# Revit family: 26-35-0095-DN40-300
name_source: partatom
category: Pipe Accessories
units: mm (PartAtom-declared; Revit-internal decimal feet)

## family parameters
Always vertical = No
Cut with Voids When Loaded = No
OmniClass Number = 23.60.00.00
OmniClass Title = General Purpose: Services
Part Type = Valve - Breaks Into
Round Connector Dimension = Use Diameter
Shared = Yes
Work Plane-Based = No

## types (10) — shared parameters
Body_Wallthickness = 15 mm  [stored 0.0492126 ft]
DN040_PN10/16 = 26-040-35-0147099
DN050_PN10/16 = 26-050-35-0147099
DN065_PN10/16 = 26-065-35-0147099
DN080_PN10/16 = 26-080-35-0147099
DN100_PN10/16 = 26-100-35-0147099
DN125_PN10/16 = 26-125-35-0147099
DN150_PN10/16 = 26-150-35-0147099
DN200_PN10 = 26-200-35-0047099
DN200_PN16 = 26-200-35-0147099
DN250_PN10 = 26-250-35-007
DN250_PN16 = 26-250-35-017
DN300_PN10 = 26-300-35-007
DN300_PN16 = 26-300-35-017
Ftc = 4 mm  [stored 0.0131234 ft]
Name_Height_reference = 10 mm  [stored 0.0328084 ft]
Rib_Height_Reference_3 = 100 mm
Rib_Thickness = 18 mm  [stored 0.0590551 ft]
Search_table = 26-35-0095-DN40-300
Tf = 26 mm
URL product pages = https://www.avkvalves.com
zero-valued in all types: Bottom_Reference

## per-type parameters (varying)
- DN 050: At=60.5 mm; Body_Height=110 mm; Body_depth=121 mm; Body_width=74 mm; Bonnet_Flange_Depth=130 mm; Bonnet_Flange_Width=90 mm; Bonnet_Flange_cut=7.5 mm  [stored 0.0246063 ft]; Bonnet_Flange_thickness=15 mm  [stored 0.0492126 ft]; Bonnet_Height=41.25 mm; Bonnet_Reference_height=100 mm; Bonnet_Thickness=75.48 mm; Bt=75.48 mm; Bt_2=68 mm; CL=56 mm; CL _Thickness=12 mm  [stored 0.0393701 ft]; CL_2=26 mm; CL_Thickness 2=20 mm  [stored 0.0656168 ft]; Cut_Reference=300 mm; DN 050=Yes; DN 065=No; DN 080=No; DN 100=No; DN 125=No; DN 150=No; DN 200=No; DN 250=No; DN 300=No; Description_=AVK_GATE_VALVE,FLANGED; F=7 mm  [stored 0.0229659 ft]; F1=8 mm  [stored 0.0262467 ft]; F2=30 mm; Fillet_Thickness=6 mm  [stored 0.019685 ft]; Flange_OR=82.5 mm; Flange_Thickness=19 mm  [stored 0.062336 ft]; Flange_Thickness_cut=28.75 mm; Ftc_reference_height=82.5 mm; Gearbox_Flange_Dia=12 mm  [stored 0.0393701 ft]; Gearbox_Flangethickness=12 mm  [stored 0.0393701 ft]; H=208 mm; H3=294 mm; Horizontal_Flange_width=172 mm; ID (Radius)=25 mm  [stored 0.082021 ft]; L=150 mm; L_Dia=50 mm; Name_Reference=90 mm; Name_Width=37 mm; Nominal Diameter (DN)=50 mm; R1tv=825 mm; R2f=15 mm  [stored 0.0492126 ft]; RF_Dia=50 mm; Rf=286.67 mm; Rib_Height_Reference_1=120 mm; Rib_Height_Reference_2=110 mm; Rib_Height_Reference_4=60 mm; Rib_Width_1=37 mm; Rib_Width_2=37 mm; Rib_Width_3=37 mm; Rib_depth_1=37 mm; Rib_depth_2=37 mm; Rib_depth_3=37 mm; Rt=275 mm
- DN 065: At=54.5 mm; Body_Height=140 mm; Body_depth=109 mm; Body_width=74 mm; Bonnet_Flange_Depth=135 mm; Bonnet_Flange_Width=85 mm; Bonnet_Flange_cut=7.5 mm  [stored 0.0246063 ft]; Bonnet_Flange_thickness=15 mm  [stored 0.0492126 ft]; Bonnet_Height=46.25 mm; Bonnet_Reference_height=130 mm; Bonnet_Thickness=75.48 mm; Bt=75.48 mm; Bt_2=68 mm; CL=59.83 mm; CL _Thickness=11.17 mm; CL_2=29.83 mm; CL_Thickness 2=18.33 mm; Cut_Reference=340 mm; DN 050=No; DN 065=Yes; DN 080=Yes; DN 100=Yes; DN 125=Yes; DN 150=Yes; DN 200=Yes; DN 250=Yes; DN 300=Yes; Description_=AVK_GATE-VALVE,FLANGED; F=8.5 mm; F1=10 mm  [stored 0.0328084 ft]; F2=34 mm; Fillet_Thickness=6 mm  [stored 0.019685 ft]; Flange_OR=92.5 mm; Flange_Thickness=19 mm  [stored 0.062336 ft]; Flange_Thickness_cut=30 mm; Ftc_reference_height=92.5 mm; Gearbox_Flange_Dia=11.17 mm; Gearbox_Flangethickness=11.17 mm; H=245 mm; H3=338 mm; Horizontal_Flange_width=186 mm; ID (Radius)=32.5 mm; L=170 mm; L_Dia=65 mm; Name_Reference=100 mm; Name_Width=37 mm; Nominal Diameter (DN)=65 mm; R1tv=925 mm; R2f=15 mm  [stored 0.0492126 ft]; RF_Dia=59 mm; Rf=310 mm; Rib_Height_Reference_1=120 mm; Rib_Height_Reference_2=110 mm; Rib_Height_Reference_4=75 mm; Rib_Width_1=37 mm; Rib_Width_2=37 mm; Rib_Width_3=37 mm; Rib_depth_1=37 mm; Rib_depth_2=37 mm; Rib_depth_3=37 mm; Rt=308.33 mm
- DN 080: At=72.5 mm; Body_Height=155 mm; Body_depth=145 mm; Body_width=79 mm; Bonnet_Flange_Depth=150 mm; Bonnet_Flange_Width=100 mm; Bonnet_Flange_cut=7.5 mm  [stored 0.0246063 ft]; Bonnet_Flange_thickness=15 mm  [stored 0.0492126 ft]; Bonnet_Height=50 mm; Bonnet_Reference_height=145 mm; Bonnet_Thickness=80.58 mm; Bt=80.58 mm; Bt_2=73 mm; CL=79.33 mm; CL _Thickness=13.67 mm; CL_2=49.33 mm; CL_Thickness 2=23.33 mm; Cut_Reference=360 mm; DN 050=Yes; DN 065=Yes; DN 080=Yes; DN 100=Yes; DN 125=Yes; DN 150=Yes; DN 200=Yes; DN 250=Yes; DN 300=Yes; Description_=AVK_GATE_VALVE,FLANGED; F=8.5 mm; F1=10 mm  [stored 0.0328084 ft]; F2=34 mm; Fillet_Thickness=6 mm  [stored 0.019685 ft]; Flange_OR=100 mm; Flange_Thickness=19 mm  [stored 0.062336 ft]; Flange_Thickness_cut=30 mm; Ftc_reference_height=100 mm; Gearbox_Flange_Dia=13.67 mm; Gearbox_Flangethickness=13.67 mm; H=282 mm; H3=382 mm; Horizontal_Flange_width=200 mm; ID (Radius)=40 mm; L=180 mm; L_Dia=80 mm; Name_Reference=130 mm; Name_Width=39.5 mm; Nominal Diameter (DN)=80 mm; R1tv=1000 mm; R2f=15 mm  [stored 0.0492126 ft]; RF_Dia=66 mm; Rf=333.33 mm; Rib_Height_Reference_1=120 mm; Rib_Height_Reference_2=110 mm; Rib_Height_Reference_4=85 mm; Rib_Width_1=39.5 mm; Rib_Width_2=39.5 mm; Rib_Width_3=39.5 mm; Rib_depth_1=39.5 mm; Rib_depth_2=39.5 mm; Rib_depth_3=39.5 mm; Rt=333.33 mm
- DN 100: At=87 mm; Body_Height=160 mm; Body_depth=174 mm; Body_width=95 mm; Bonnet_Flange_Depth=180 mm; Bonnet_Flange_Width=122 mm; Bonnet_Flange_cut=7.5 mm  [stored 0.0246063 ft]; Bonnet_Flange_thickness=15 mm  [stored 0.0492126 ft]; Bonnet_Height=55 mm; Bonnet_Reference_height=150 mm; Bonnet_Thickness=96.9 mm; Bt=96.9 mm; Bt_2=89 mm; CL=89.67 mm; CL _Thickness=17.33 mm; CL_2=59.67 mm; CL_Thickness 2=30.67 mm; Cut_Reference=380 mm; DN 050=Yes; DN 065=Yes; DN 080=Yes; DN 100=Yes; DN 125=Yes; DN 150=Yes; DN 200=Yes; DN 250=Yes; DN 300=Yes; Description_=AVK_GATE_VALVE,FLANGED; F=9.5 mm  [stored 0.031168 ft]; F1=11 mm  [stored 0.0360892 ft]; F2=38 mm; Fillet_Thickness=6 mm  [stored 0.019685 ft]; Flange_OR=110 mm; Flange_Thickness=19 mm  [stored 0.062336 ft]; Flange_Thickness_cut=30 mm; Ftc_reference_height=110 mm; Gearbox_Flange_Dia=17.33 mm; Gearbox_Flangethickness=17.33 mm; H=305 mm; H3=415 mm; Horizontal_Flange_width=220 mm; ID (Radius)=50 mm; L=190 mm; L_Dia=100 mm; Name_Reference=150 mm; Name_Width=47.5 mm; Nominal Diameter (DN)=100 mm; R1tv=1100 mm; R2f=15 mm  [stored 0.0492126 ft]; RF_Dia=78 mm; Rf=366.67 mm; Rib_Height_Reference_1=120 mm; Rib_Height_Reference_2=110 mm; Rib_Height_Reference_4=90 mm; Rib_Width_1=47.5 mm; Rib_Width_2=47.5 mm; Rib_Width_3=47.5 mm; Rib_depth_1=47.5 mm; Rib_depth_2=47.5 mm; Rib_depth_3=47.5 mm; Rt=366.67 mm
- DN 150: At=123 mm; Body_Height=210 mm; Body_depth=246 mm; Body_width=100 mm; Bonnet_Flange_Depth=255 mm; Bonnet_Flange_Width=124 mm; Bonnet_Flange_cut=7.5 mm  [stored 0.0246063 ft]; Bonnet_Flange_thickness=15 mm  [stored 0.0492126 ft]; Bonnet_Height=71.25 mm; Bonnet_Reference_height=200 mm; Bonnet_Thickness=102 mm; Bt=102 mm; Bt_2=94 mm; CL=134.33 mm; CL _Thickness=17.67 mm; CL_2=104.33 mm; CL_Thickness 2=31.33 mm; Cut_Reference=420 mm; DN 050=Yes; DN 065=Yes; DN 080=Yes; DN 100=Yes; DN 125=Yes; DN 150=Yes; DN 200=Yes; DN 250=Yes; DN 300=Yes; Description_=AVK_GATE_VALVE,FLANGED; F=9.5 mm  [stored 0.031168 ft]; F1=11 mm  [stored 0.0360892 ft]; F2=38 mm; Fillet_Thickness=12 mm  [stored 0.0393701 ft]; Flange_OR=142.5 mm; Flange_Thickness=19 mm  [stored 0.062336 ft]; Flange_Thickness_cut=33.75 mm; Ftc_reference_height=142.5 mm; Gearbox_Flange_Dia=17.67 mm; Gearbox_Flangethickness=17.67 mm; H=400 mm; H3=543 mm; Horizontal_Flange_width=286 mm; ID (Radius)=75 mm; L=210 mm; L_Dia=150 mm; Name_Reference=170 mm; Name_Width=50 mm; Nominal Diameter (DN)=150 mm; R1tv=1425 mm; R2f=30 mm; RF_Dia=106 mm; Rf=476.67 mm; Rib_Height_Reference_1=120 mm; Rib_Height_Reference_2=110 mm; Rib_Height_Reference_4=150 mm; Rib_Width_1=50 mm; Rib_Width_2=50 mm; Rib_Width_3=50 mm; Rib_depth_1=50 mm; Rib_depth_2=50 mm; Rib_depth_3=50 mm; Rt=475 mm
- DN 200: At=150 mm; Body_Height=270 mm; Body_depth=300 mm; Body_width=115 mm; Bonnet_Flange_Depth=320 mm; Bonnet_Flange_Width=135 mm; Bonnet_Flange_cut=12.5 mm  [stored 0.0410105 ft]; Bonnet_Flange_thickness=25 mm  [stored 0.082021 ft]; Bonnet_Height=85 mm; Bonnet_Reference_height=260 mm; Bonnet_Thickness=117.3 mm; Bt=117.3 mm; Bt_2=109 mm; CL=158.5 mm; CL _Thickness=19.5 mm  [stored 0.0639764 ft]; CL_2=128.5 mm; CL_Thickness 2=35 mm; Cut_Reference=460 mm; DN 050=Yes; DN 065=Yes; DN 080=Yes; DN 100=Yes; DN 125=Yes; DN 150=Yes; DN 200=Yes; DN 250=Yes; DN 300=Yes; Description_=AVK_GATE_VALVE,FLANGED; F=12 mm  [stored 0.0393701 ft]; F1=14 mm  [stored 0.0459318 ft]; F2=42 mm; Fillet_Thickness=24 mm  [stored 0.0787402 ft]; Flange_OR=170 mm; Flange_Thickness=20 mm  [stored 0.0656168 ft]; Flange_Thickness_cut=35 mm; Ftc_reference_height=170 mm; Gearbox_Flange_Dia=19.5 mm  [stored 0.0639764 ft]; Gearbox_Flangethickness=19.5 mm  [stored 0.0639764 ft]; H=490 mm; H3=660 mm; Horizontal_Flange_width=340 mm; ID (Radius)=100 mm; L=230 mm; L_Dia=200 mm; Name_Reference=200 mm; Name_Width=57.5 mm; Nominal Diameter (DN)=200 mm; R1tv=1700 mm; R2f=60 mm; RF_Dia=133 mm; Rf=566.67 mm; Rib_Height_Reference_1=120 mm; Rib_Height_Reference_2=110 mm; Rib_Height_Reference_4=180 mm; Rib_Width_1=57.5 mm; Rib_Width_2=57.5 mm; Rib_Width_3=57.5 mm; Rib_depth_1=57.5 mm; Rib_depth_2=57.5 mm; Rib_depth_3=57.5 mm; Rt=566.67 mm
- DN 250: At=175 mm; Body_Height=380 mm; Body_depth=350 mm; Body_width=140 mm; Bonnet_Flange_Depth=372 mm; Bonnet_Flange_Width=162 mm; Bonnet_Flange_cut=12.5 mm  [stored 0.0410105 ft]; Bonnet_Flange_thickness=25 mm  [stored 0.082021 ft]; Bonnet_Height=100 mm; Bonnet_Reference_height=370 mm; Bonnet_Thickness=142.8 mm; Bt=142.8 mm; Bt_2=134 mm; CL=213 mm; CL _Thickness=24 mm  [stored 0.0787402 ft]; CL_2=183 mm; CL_Thickness 2=44 mm; Cut_Reference=500 mm; DN 050=Yes; DN 065=Yes; DN 080=Yes; DN 100=Yes; DN 125=Yes; DN 150=Yes; DN 200=Yes; DN 250=Yes; DN 300=Yes; Description_=AVK_GATE_VALVE,FLANGED; F=13.5 mm  [stored 0.0442913 ft]; F1=15.5 mm  [stored 0.050853 ft]; F2=47 mm; Fillet_Thickness=24 mm  [stored 0.0787402 ft]; Flange_OR=200 mm; Flange_Thickness=22 mm  [stored 0.0721785 ft]; Flange_Thickness_cut=37.5 mm; Ftc_reference_height=200 mm; Gearbox_Flange_Dia=24 mm  [stored 0.0787402 ft]; Gearbox_Flangethickness=24 mm  [stored 0.0787402 ft]; H=664 mm; H3=864 mm; Horizontal_Flange_width=400 mm; ID (Radius)=125 mm; L=250 mm; L_Dia=250 mm; Name_Reference=200 mm; Name_Width=70 mm; Nominal Diameter (DN)=250 mm; R1tv=2000 mm; R2f=60 mm; RF_Dia=160 mm; Rf=666.67 mm; Rib_Height_Reference_1=90 mm; Rib_Height_Reference_2=110 mm; Rib_Height_Reference_4=250 mm; Rib_Width_1=170 mm; Rib_Width_2=70 mm; Rib_Width_3=70 mm; Rib_depth_1=358 mm; Rib_depth_2=70 mm; Rib_depth_3=70 mm; Rt=666.67 mm
- DN 300: At=206 mm; Body_Height=430 mm; Body_depth=412 mm; Body_width=160 mm; Bonnet_Flange_Depth=438 mm; Bonnet_Flange_Width=196 mm; Bonnet_Flange_cut=17.5 mm  [stored 0.0574147 ft]; Bonnet_Flange_thickness=35 mm; Bonnet_Height=113.75 mm; Bonnet_Reference_height=420 mm; Bonnet_Thickness=163.2 mm; Bt=163.2 mm; Bt_2=154 mm; CL=225 mm; CL _Thickness=29.67 mm; CL_2=195 mm; CL_Thickness 2=55.33 mm; Cut_Reference=540 mm; DN 050=Yes; DN 065=Yes; DN 080=Yes; DN 100=Yes; DN 125=Yes; DN 150=Yes; DN 200=Yes; DN 250=Yes; DN 300=Yes; Description_=AVK_GATE_VALVE,FLANGED; F=13.5 mm  [stored 0.0442913 ft]; F1=15.5 mm  [stored 0.050853 ft]; F2=55 mm; Fillet_Thickness=24 mm  [stored 0.0787402 ft]; Flange_OR=227.5 mm; Flange_Thickness=24.5 mm  [stored 0.0803806 ft]; Flange_Thickness_cut=38.75 mm; Ftc_reference_height=227.5 mm; Gearbox_Flange_Dia=29.67 mm; Gearbox_Flangethickness=30 mm; H=740 mm; H3=968 mm; Horizontal_Flange_width=456 mm; ID (Radius)=150 mm; L=270 mm; L_Dia=300 mm; Name_Reference=300 mm; Name_Width=80 mm; Nominal Diameter (DN)=300 mm; R1tv=2275 mm; R2f=60 mm; RF_Dia=185 mm; Rf=760 mm; Rib_Height_Reference_1=113 mm; Rib_Height_Reference_2=285 mm; Rib_Height_Reference_4=325 mm; Rib_Width_1=196 mm; Rib_Width_2=196 mm; Rib_Width_3=80 mm; Rib_depth_1=438 mm; Rib_depth_2=438 mm; Rib_depth_3=80 mm; Rt=758.33 mm
- DN 125: At=109 mm; Body_Height=170 mm; Body_depth=218 mm; Body_width=100 mm; Bonnet_Flange_Depth=235 mm; Bonnet_Flange_Width=120 mm; Bonnet_Flange_cut=7.5 mm  [stored 0.0246063 ft]; Bonnet_Flange_thickness=15 mm  [stored 0.0492126 ft]; Bonnet_Height=62.5 mm; Bonnet_Reference_height=160 mm; Bonnet_Thickness=102 mm; Bt=102 mm; Bt_2=94 mm; CL=121 mm; CL _Thickness=17 mm  [stored 0.0557743 ft]; CL_2=91 mm; CL_Thickness 2=30 mm; Cut_Reference=400 mm; DN 050=Yes; DN 065=Yes; DN 080=Yes; DN 100=Yes; DN 125=Yes; DN 150=Yes; DN 200=Yes; DN 250=Yes; DN 300=Yes; Description_=AVK_GATE_VALVE,FLANGED; F=9.5 mm  [stored 0.031168 ft]; F1=11 mm  [stored 0.0360892 ft]; F2=38 mm; Fillet_Thickness=6 mm  [stored 0.019685 ft]; Flange_OR=125 mm; Flange_Thickness=19 mm  [stored 0.062336 ft]; Flange_Thickness_cut=31.25 mm; Ftc_reference_height=125 mm; Gearbox_Flange_Dia=17 mm  [stored 0.0557743 ft]; Gearbox_Flangethickness=17 mm  [stored 0.0557743 ft]; H=346 mm; H3=471 mm; Horizontal_Flange_width=250 mm; ID (Radius)=62.5 mm; L=200 mm; L_Dia=125 mm; Name_Reference=165 mm; Name_Width=50 mm; Nominal Diameter (DN)=125 mm; R1tv=1250 mm; R2f=15 mm  [stored 0.0492126 ft]; RF_Dia=92 mm; Rf=416.67 mm; Rib_Height_Reference_1=120 mm; Rib_Height_Reference_2=110 mm; Rib_Height_Reference_4=120 mm; Rib_Width_1=50 mm; Rib_Width_2=50 mm; Rib_Width_3=50 mm; Rib_depth_1=50 mm; Rib_depth_2=50 mm; Rib_depth_3=50 mm; Rt=416.67 mm
- DN 040: At=55.5 mm; Body_Height=100 mm; Body_depth=111 mm; Body_width=70 mm; Bonnet_Flange_Depth=128 mm; Bonnet_Flange_Width=80 mm; Bonnet_Flange_cut=7.5 mm  [stored 0.0246063 ft]; Bonnet_Flange_thickness=15 mm  [stored 0.0492126 ft]; Bonnet_Height=37.5 mm; Bonnet_Reference_height=90 mm; Bonnet_Thickness=71.4 mm; Bt=71.4 mm; Bt_2=64 mm; CL=54.67 mm; CL _Thickness=10.33 mm; CL_2=24.67 mm; CL_Thickness 2=16.67 mm; Cut_Reference=280 mm; DN 050=Yes; DN 065=No; DN 080=No; DN 100=No; DN 125=No; DN 150=No; DN 200=No; DN 250=No; DN 300=No; Description_=AVK_GATE_VALVE,FLANGED; F=7 mm  [stored 0.0229659 ft]; F1=8 mm  [stored 0.0262467 ft]; F2=30 mm; Fillet_Thickness=6 mm  [stored 0.019685 ft]; Flange_OR=75 mm; Flange_Thickness=19 mm  [stored 0.062336 ft]; Flange_Thickness_cut=27.5 mm  [stored 0.0902231 ft]; Ftc_reference_height=75 mm; Gearbox_Flange_Dia=10.33 mm; Gearbox_Flangethickness=10.33 mm; H=195 mm; H3=275 mm; Horizontal_Flange_width=160 mm; ID (Radius)=20 mm  [stored 0.0656168 ft]; L=140 mm; L_Dia=40 mm; Name_Reference=80 mm; Name_Width=35 mm; Nominal Diameter (DN)=40 mm; R1tv=750 mm; R2f=15 mm  [stored 0.0492126 ft]; RF_Dia=40 mm; Rf=266.67 mm; Rib_Height_Reference_1=120 mm; Rib_Height_Reference_2=110 mm; Rib_Height_Reference_4=60 mm; Rib_Width_1=35 mm; Rib_Width_2=35 mm; Rib_Width_3=35 mm; Rib_depth_1=35 mm; Rib_depth_2=35 mm; Rib_depth_3=35 mm; Rt=250 mm

note: [stored X ft] marks values corroborated as IEEE doubles in the binary element streams (Revit-internal decimal feet)

## geometry (parser evidence)
native form markers: Sweep x6
no freeform markers — native parametric forms only
